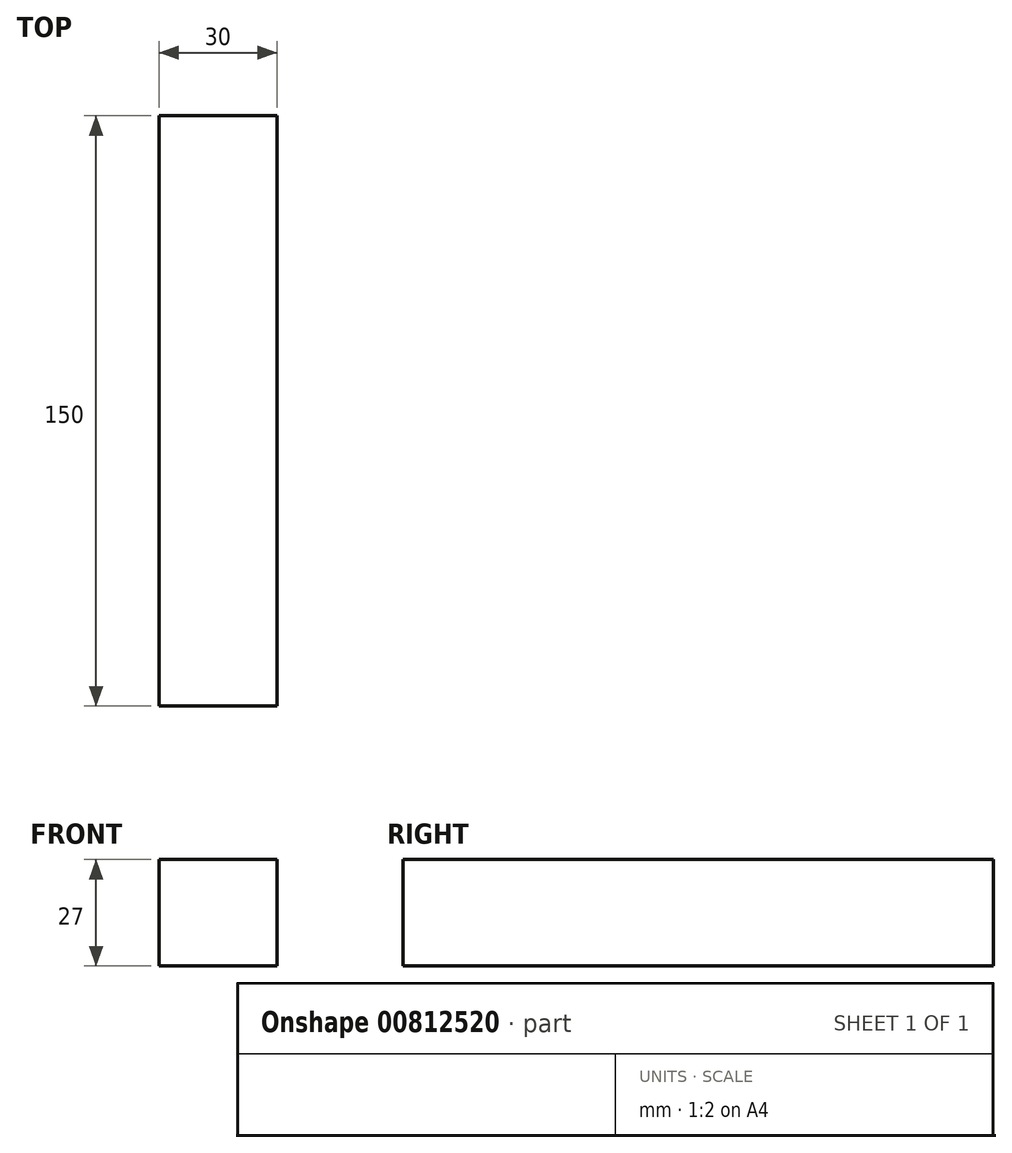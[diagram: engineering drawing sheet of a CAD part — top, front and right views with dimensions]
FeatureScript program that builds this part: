
annotation { "Feature Type Name" : "Feature", "Feature Type Description" : "" }
export const myFeature = defineFeature(function(context is Context, id is Id, definition is map)
    precondition{}
    {
        {
            var Q0;
            Q0=qCreatedBy(makeId("Front.planeOp"),FACE);
            var sketch = newSketch(context, id + "F0", { "sketchPlane" : qUnion([Q0])});
            skLineSegment(sketch, "E0.bottom", {"start": v(-10.34, 36.12) * mm, "end": v(19.66, 36.12) * mm});
            skLineSegment(sketch, "E0.top", {"start": v(-10.34, 9.12) * mm, "end": v(19.66, 9.12) * mm});
            skLineSegment(sketch, "E0.left", {"start": v(-10.34, 36.12) * mm, "end": v(-10.34, 9.12) * mm});
            skLineSegment(sketch, "E0.right", {"start": v(19.66, 36.12) * mm, "end": v(19.66, 9.12) * mm});
            skSolve(sketch);
        }
        {
            var Q0;
            Q0=makeQuery(id+"F0.imprint","IMPRINT",FACE,{"disambiguationData":[TD([[makeQuery(id+"F0.imprint","IMPRINT",EDGE,{"derivedFrom":sQuery(id+"F0.wireOp",EDGE,"E0.bottom")}),-1.0]])]});
            extrude(context, id + "F1", {"entities" : qUnion([Q0]), "depth" : 150 * mm, "offsetDistance" : 25 * mm});
        }
    });
